# Revit family: Haworth_MeetingPoints_Table_Square_EU_PRELIMINARY
name_source: partatom
category: Furniture
units: mm (PartAtom-declared; Revit-internal decimal feet)

## family parameters
Always vertical = Yes
Cut with Voids When Loaded = No
OmniClass Number = 23.40.70.14.64.21
OmniClass Title = Systems Furniture
Room Calculation Point = No
Shared = No
Work Plane-Based = No

## types (7) — shared parameters
Assembly Code = E2020200
Description = Haworth - Meeting Points - Table - Square
Glide Finish = Haworth _ Polymer _ Black
Manufacturer = Haworth
Max. Height = 110 cm
Max. Width = 100 cm
Min. Height = 74 cm
Min. Width = 70 cm
Model = A00000002
Revision Number = 1
Size = Verify Final Dim. w/ Haworth
Standard Widths = 70, 80, 90, 100 cm
URL = https://www.haworth.com
URL - Product = https://www.haworth.com
Warranty = http://www.haworth.com

## per-type parameters (varying)
| type | Actual Depth | Actual Height | Actual Width | Base Height | Casters | Four Star Base | Glides | Height | Large | Small | Square Base Support |
| 70cm x 74h - with Casters | 70 cm | 74 cm | 70 cm | 71 cm | Yes | Yes | No | 74 cm | No | Yes | No |
| 80cm x 110h - with Glides | 80 cm | 110 cm | 80 cm | 107 cm | No | Yes | Yes | 110 cm | No | No | No |
| 90cm x 74h - with Casters | 90 cm | 74 cm | 90 cm | 71 cm | Yes | Yes | No | 74 cm | No | No | No |
| 100cm x 110h - with Glides | 100 cm | 110 cm | 100 cm | 107 cm | No | Yes | Yes | 110 cm | No | No | No |
| 90cm x 74h - with Glides | 90 cm | 74 cm | 90 cm | 71 cm | No | Yes | Yes | 74 cm | No | No | No |
| 70cm x 110h - with Square Base | 70 cm | 110 cm | 70 cm | 107 cm | No | No | No | 110 cm | No | Yes | Yes |
| 100cm x 74h - with Square Base | 100 cm | 74 cm | 100 cm | 71 cm | No | No | No | 74 cm | Yes | No | Yes |

## geometry (parser evidence)
native form markers: Blend x8, Sweep x18
no freeform markers — native parametric forms only
